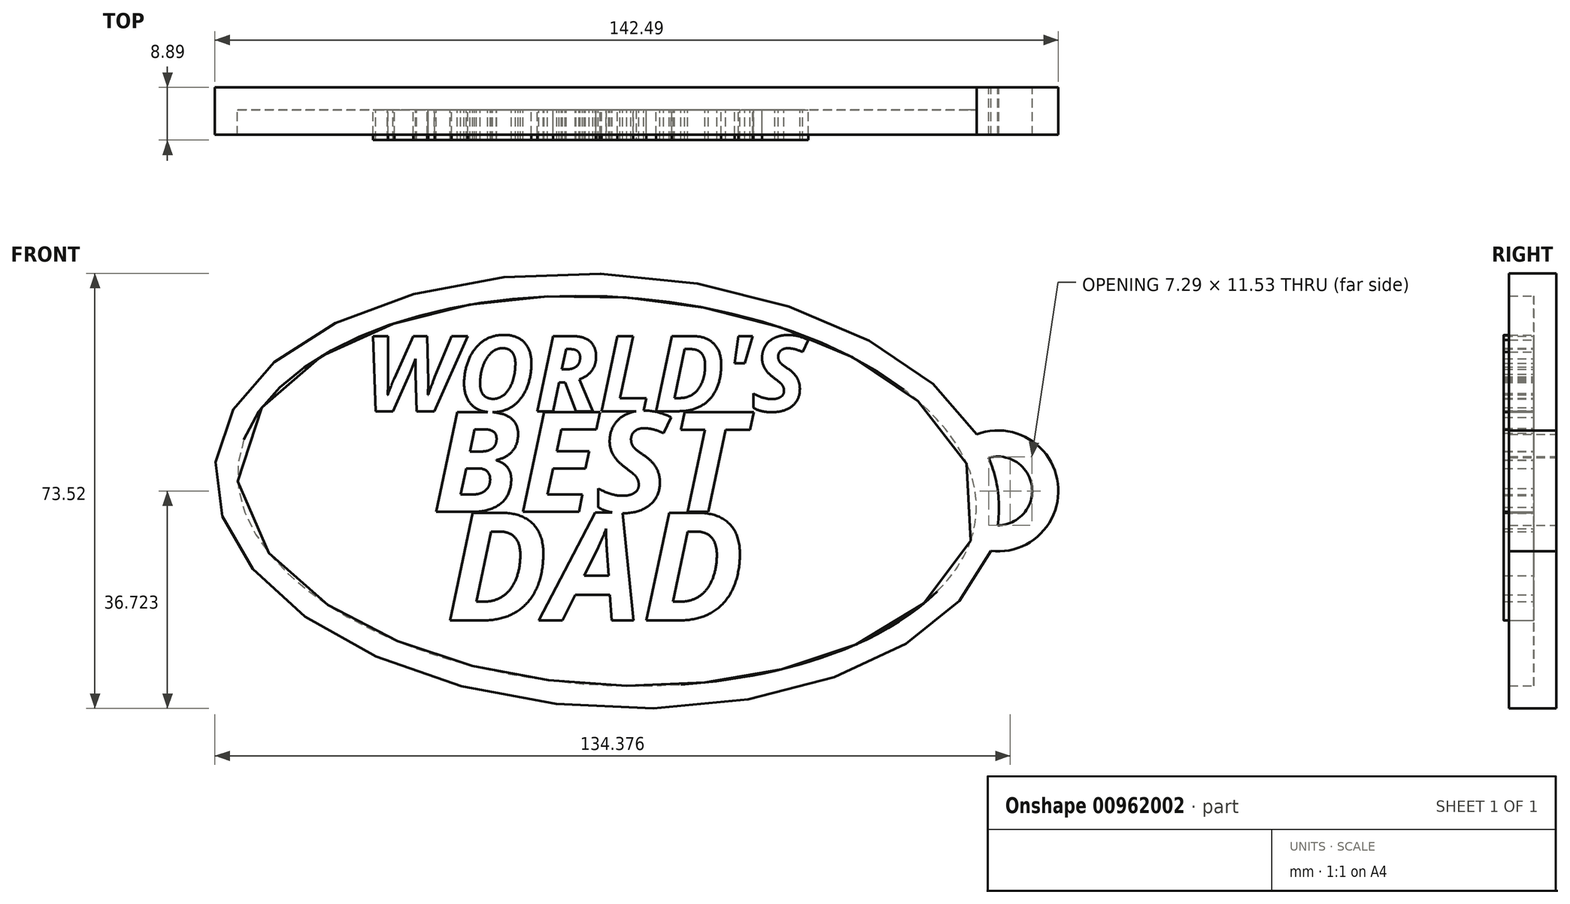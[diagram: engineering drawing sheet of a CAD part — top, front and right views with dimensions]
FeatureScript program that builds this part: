
annotation { "Feature Type Name" : "Feature", "Feature Type Description" : "" }
export const myFeature = defineFeature(function(context is Context, id is Id, definition is map)
    precondition{}
    {
        {
            var Q0;
            Q0=qCreatedBy(makeId("Front.planeOp"),FACE);
            var sketch = newSketch(context, id + "F0", { "sketchPlane" : qUnion([Q0])});
            skEllipticalArc(sketch, "E0", {});
            skArc(sketch, "E1", {"start": v(64.86, -10.15) * mm, "mid": v(76.18, 1.24) * mm, "end": v(62.45, 9.57) * mm});
            skArc(sketch, "E2", {"start": v(66, -5.8) * mm, "mid": v(71.8, 0.76) * mm, "end": v(64.5, 5.6) * mm});
            skEllipticalArc(sketch, "E3.trimOffspring", {});
            const initialGuessF0  = {"E0": [0, 0, 0.9981656577365403, -0.060541883976136676, 0.06631141120487914, 0.03661107601537537, 0.37279495973874477, 6.112819501547151], "E3.trimOffspring": [0, 0, 0.9981656577365403, -0.060541883976136676, 0.06631141120487914, 0.03661107601537537, 6.234080340130208, 0.2622562890357806]};
            skSetInitialGuess(sketch, initialGuessF0);
            skSolve(sketch);
        }
        {
            var Q0;
            Q0 = qSketchRegion(id + "F0", true);
            extrude(context, id + "F1", {"entities" : qUnion([Q0]), "depth" : 8 * mm, "offsetDistance" : 25.4 * mm});
        }
        {
            var Q0;
            Q0=makeQuery(id+"F1.opExtrude","CAP_FACE",FACE,{"disambiguationData":[OSD([sQuery(id+"F0.wireOp",EDGE,"E0"),sQuery(id+"F0.wireOp",EDGE,"E1"),sQuery(id+"F0.wireOp",EDGE,"E2")])],"isStart":false});
            shell(context, id + "F2", {"entities" : qUnion([Q0]), "thickness" : 3.8 * mm});
        }
        {
            var Q0;
            Q0=qCreatedBy(makeId("Front.planeOp"),FACE);
            var sketch = newSketch(context, id + "F3", { "sketchPlane" : qUnion([Q0])});
            skText(sketch, "E4", { "text": "WORLD\'S", "fontName": "OpenSans-BoldItalic.ttf"});
            skText(sketch, "E5", { "text": "BEST", "fontName": "OpenSans-BoldItalic.ttf"});
            skText(sketch, "E6", { "text": "DAD\n", "fontName": "OpenSans-BoldItalic.ttf"});
            const initialGuessF3  = {"E4": [-0.04109, 0.01346, 1, 0, 0.0128], "E5": [-0.02945, -0.00355, 1, 0, 0.01702], "E6": [-0.02718, -0.02188, 1, 0, 0.01832]};
            skSetInitialGuess(sketch, initialGuessF3);
            skSolve(sketch);
        }
        {
            var Q0;
            Q0 = qSketchRegion(id + "F3", true);
            extrude(context, id + "F4", {"entities" : qUnion([Q0]), "operationType" : NewBodyOperationType.ADD, "depth" : 8.9 * mm, "offsetDistance" : 25.4 * mm});
        }
    });
